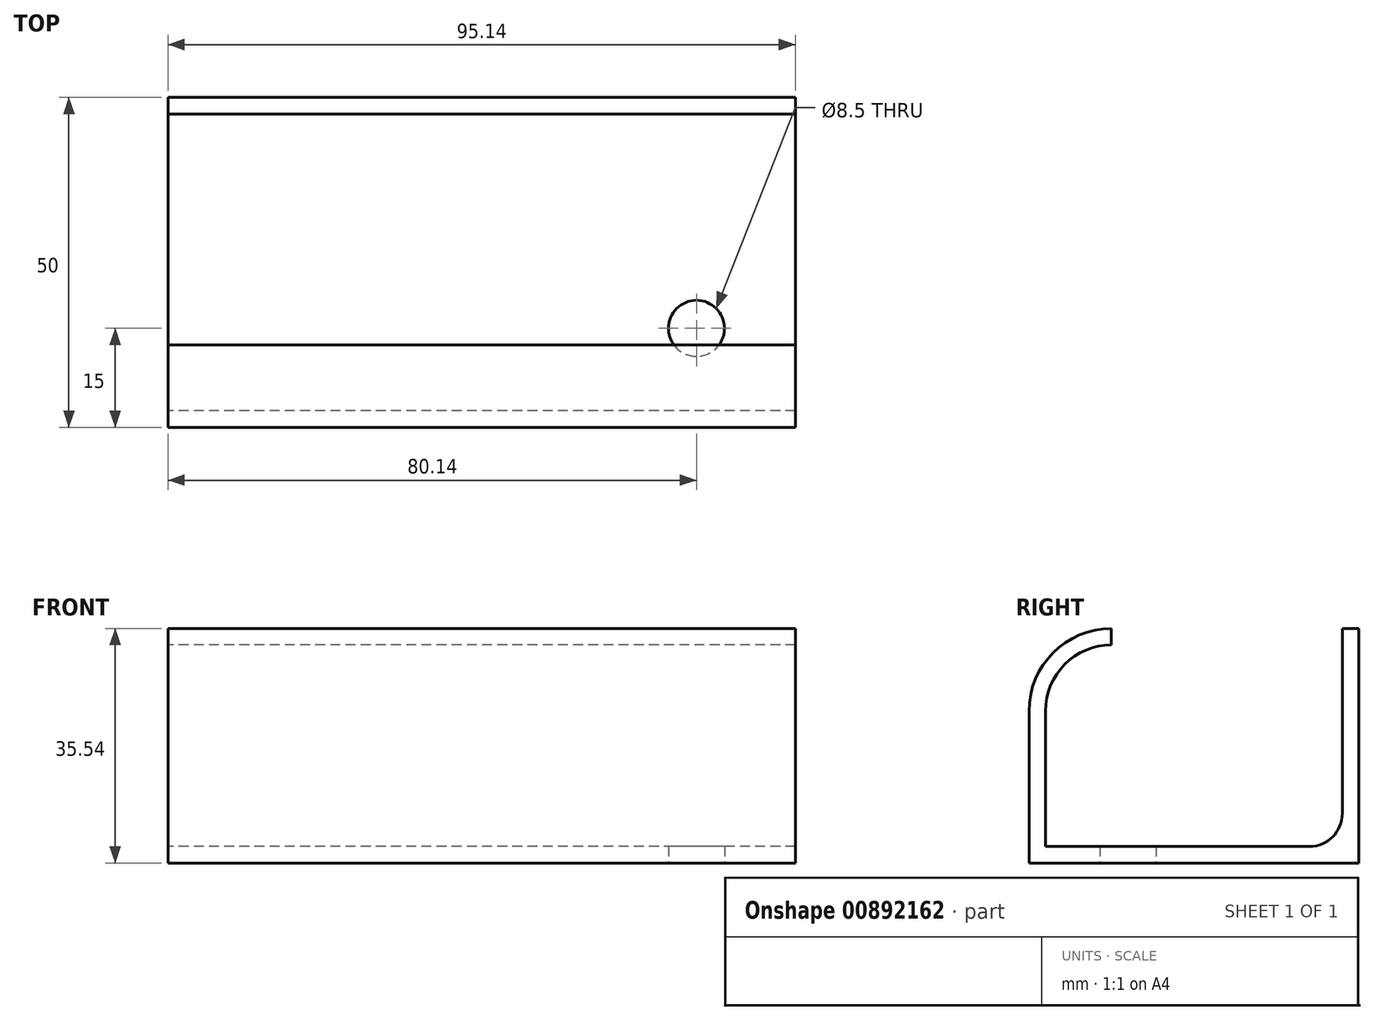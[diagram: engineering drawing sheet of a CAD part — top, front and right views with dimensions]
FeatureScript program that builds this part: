
annotation { "Feature Type Name" : "Feature", "Feature Type Description" : "" }
export const myFeature = defineFeature(function(context is Context, id is Id, definition is map)
    precondition{}
    {
        {
            var Q0;
            Q0=qCreatedBy(makeId("Front.planeOp"),FACE);
            var sketch = newSketch(context, id + "F0", { "sketchPlane" : qUnion([Q0])});
            skLineSegment(sketch, "E0.bottom", {"start": v(32.84, 21.51) * mm, "end": v(-62.3, 21.51) * mm});
            skLineSegment(sketch, "E0.top", {"start": v(32.84, 57.05) * mm, "end": v(-62.3, 57.05) * mm});
            skLineSegment(sketch, "E0.left", {"start": v(32.84, 21.51) * mm, "end": v(32.84, 57.05) * mm});
            skLineSegment(sketch, "E0.right", {"start": v(-62.3, 21.51) * mm, "end": v(-62.3, 57.05) * mm});
            skSolve(sketch);
        }
        {
            var Q0;
            Q0=makeQuery(id+"F0.imprint","IMPRINT",FACE,{"disambiguationData":[TD([[makeQuery(id+"F0.imprint","IMPRINT",EDGE,{"derivedFrom":sQuery(id+"F0.wireOp",EDGE,"E0.bottom")}),-1.0]])]});
            extrude(context, id + "F1", {"entities" : qUnion([Q0]), "oppositeDirection" : true, "depth" : 50 * mm, "offsetDistance" : 25 * mm});
        }
        {
            var Q0;
            Q0=makeQuery(id+"F1.opExtrude","CAP_EDGE",EDGE,{"disambiguationData":[OSD([sQuery(id+"F0.wireOp",EDGE,"E0.top")])],"isStart":true});
            fillet(context, id + "F2", {"entities" : qUnion([Q0]), "radius" : 12.5 * mm, "tangentPropagation" : true, "allowEdgeOverflow" : false});
        }
        {
            var Q0;
            Q0=makeQuery(id+"F1.opExtrude","SWEPT_FACE",FACE,{"disambiguationData":[OSD([sQuery(id+"F0.wireOp",EDGE,"E0.left")])]});
            var Q1;
            Q1=makeQuery(id+"F1.opExtrude","SWEPT_FACE",FACE,{"disambiguationData":[OSD([sQuery(id+"F0.wireOp",EDGE,"E0.top")])]});
            var Q2;
            Q2=makeQuery(id+"F1.opExtrude","SWEPT_FACE",FACE,{"disambiguationData":[OSD([sQuery(id+"F0.wireOp",EDGE,"E0.right")])]});
            shell(context, id + "F3", {"entities" : qUnion([Q0, Q1, Q2]), "thickness" : 2.5 * mm});
        }
        {
            var Q0;
            {var subQ0=sQuery(id+"F0.wireOp",EDGE,"E0.bottom");Q0=makeQuery(id+"F3.opShell","OFFSET_EDGE",EDGE,{"disambiguationData":[OSD([subQ0]),TDD([makeQuery(id+"F1.opExtrude","CAP_EDGE",EDGE,{"disambiguationData":[OSD([subQ0])],"isStart":false})])]});}
            fillet(context, id + "F4", {"entities" : qUnion([Q0]), "radius" : 5 * mm, "tangentPropagation" : true, "allowEdgeOverflow" : false});
        }
        {
            var Q0;
            Q0=makeQuery(id+"F1.opExtrude","SWEPT_FACE",FACE,{"disambiguationData":[OSD([sQuery(id+"F0.wireOp",EDGE,"E0.bottom")])]});
            var sketch = newSketch(context, id + "F5", { "sketchPlane" : qUnion([Q0])});
            skCircle(sketch, "E1", {"center": v(17.84, -15) * mm, "radius": 4.25 * mm});
            skSolve(sketch);
        }
        {
            var Q0;
            Q0=makeQuery(id+"F5.imprint","IMPRINT",FACE,{"disambiguationData":[TD([[makeQuery(id+"F5.imprint","IMPRINT",EDGE,{"derivedFrom":sQuery(id+"F5.wireOp",EDGE,"E1")}),1.0]])]});
            extrude(context, id + "F6", {"entities" : qUnion([Q0]), "operationType" : NewBodyOperationType.REMOVE, "oppositeDirection" : true, "depth" : 25 * mm, "offsetDistance" : 25 * mm});
        }
    });
